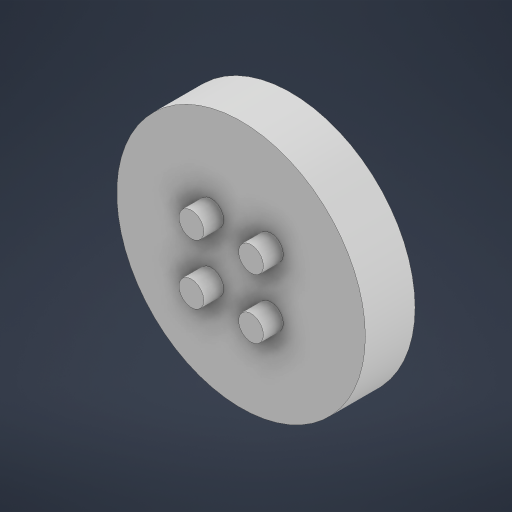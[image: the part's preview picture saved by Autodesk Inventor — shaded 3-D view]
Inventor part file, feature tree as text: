
AUTODESK INVENTOR PART (.ipt)
format: ipt  version: 2024 (Build 280153000, 153)  size: 200,192 bytes
history: native  units: mm
features: extrude x2, sketch x2, other x1
ambient origin geometry x8: Origin, YZ Plane, XZ Plane, XY Plane, X Axis, Y Axis, Z Axis, Center Point
bodies: Body1 (feature_tree)
feature tree (5):
  other  "Sólido1"
  extrude  "Extrusión1"  Depth=10.0mm TaperAngle=0.0deg
  extrude  "Extrusión2"  Depth=4.0mm
  sketch  "Boceto1"  dims[d0=50.0mm d1=10.0mm d2=0.0mm]
  sketch  "Boceto3"  dims[d3=5.0mm d4=6.0mm d5=6.0mm d6=40.0mm d8=360.0deg d10=4.0mm d11=0.0mm d12=44.0mm d13=36.0mm d14=18.0mm d16=22.0mm]
